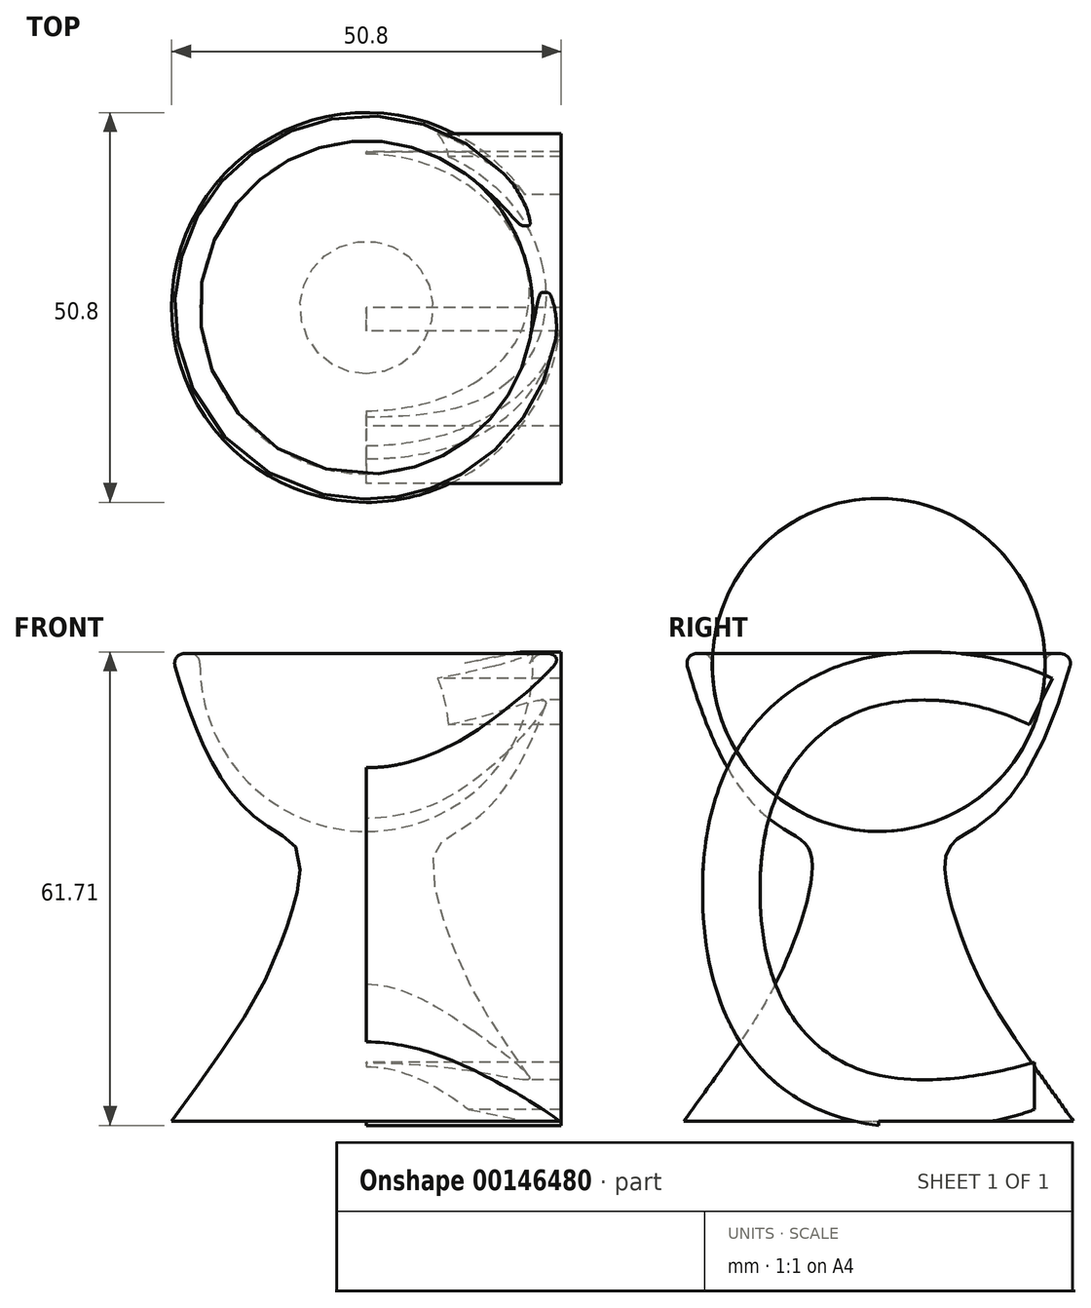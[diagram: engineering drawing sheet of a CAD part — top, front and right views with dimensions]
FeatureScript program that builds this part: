
annotation { "Feature Type Name" : "Feature", "Feature Type Description" : "" }
export const myFeature = defineFeature(function(context is Context, id is Id, definition is map)
    precondition{}
    {
        {
            var Q0;
            Q0=qCreatedBy(makeId("Top.planeOp"),FACE);
            var sketch = newSketch(context, id + "F0", { "sketchPlane" : qUnion([Q0])});
            skCircle(sketch, "E0", {"center": v(0, 0) * mm, "radius": 25.4 * mm});
            skSolve(sketch);
        }
        {
            var Q0;
            Q0 = qSketchRegion(id + "F0", true);
            extrude(context, id + "F1", {"entities" : qUnion([Q0]), "depth" : 60.96 * mm});
        }
        {
            var Q0;
            Q0=qCreatedBy(makeId("Front.planeOp"),FACE);
            var sketch = newSketch(context, id + "F2", { "sketchPlane" : qUnion([Q0])});
            skLineSegment(sketch, "E1", {"start": v(-25.4, 67.56) * mm, "end": v(-25.4, -5.64) * mm});
            skLineSegment(sketch, "E2", {"start": v(0, 70.59) * mm, "end": v(0, -29.87) * mm, "construction": true});
            skLineSegment(sketch, "E3", {"start": v(-48.12, 60.96) * mm, "end": v(45.26, 60.96) * mm, "construction": true});
            skFitSpline(sketch, "E4", {"points": [v(-25.4, 60.96) * mm, v(-8.92, 35.08) * mm, v(-11.78, 21.62) * mm, v(-25.4, 0) * mm], "startDerivative": vector(51.75, -193.24) * mm, "endDerivative": vector(-75.06, -104.5) * mm});
            skLineSegment(sketch, "E5", {"start": v(-25.4, 60.96) * mm, "end": v(-25.4, 0) * mm});
            skSolve(sketch);
        }
        {
            var Q0;
            Q0 = qSketchRegion(id + "F2", true);
            var Q1;
            Q1=sQuery(id+"F2.wireOp",EDGE,"E2");
            revolve(context, id + "F3", {"operationType" : NewBodyOperationType.REMOVE, "entities" : qUnion([Q0]), "axis" : qUnion([Q1]), "revolveType" : RevolveType.FULL, "oppositeDirection" : true});
        }
        {
            var Q0;
            Q0=qCreatedBy(makeId("Right.planeOp"),FACE);
            var sketch = newSketch(context, id + "F4", { "sketchPlane" : qUnion([Q0])});
            skText(sketch, "E6", { "text": "C", "fontName": "OpenSans-Regular.ttf"});
            const initialGuessF4  = {"E6": [-0.02813, 0, 1, 0, 0.06083]};
            skSetInitialGuess(sketch, initialGuessF4);
            skSolve(sketch);
        }
        {
            var Q0;
            Q0 = qSketchRegion(id + "F4", true);
            extrude(context, id + "F5", {"entities" : qUnion([Q0]), "operationType" : NewBodyOperationType.ADD, "depth" : 25.4 * mm});
        }
        {
            var Q0;
            Q0=qCreatedBy(makeId("Front.planeOp"),FACE);
            var sketch = newSketch(context, id + "F6", { "sketchPlane" : qUnion([Q0])});
            skLineSegment(sketch, "E7.bottom", {"start": v(-32.81, -11.53) * mm, "end": v(31.47, -11.53) * mm});
            skLineSegment(sketch, "E7.top", {"start": v(-32.81, 0) * mm, "end": v(31.47, 0) * mm});
            skLineSegment(sketch, "E7.left", {"start": v(-32.81, -11.53) * mm, "end": v(-32.81, 0) * mm});
            skLineSegment(sketch, "E7.right", {"start": v(31.47, -11.53) * mm, "end": v(31.47, 0) * mm});
            skSolve(sketch);
        }
        {
            var Q0;
            Q0=makeQuery(id+"F6.imprint","IMPRINT",FACE,{"disambiguationData":[TD([[makeQuery(id+"F6.imprint","IMPRINT",EDGE,{"derivedFrom":sQuery(id+"F6.wireOp",EDGE,"E7.bottom")}),1.0]])]});
            extrude(context, id + "F7", {"entities" : qUnion([Q0]), "operationType" : NewBodyOperationType.REMOVE, "oppositeDirection" : true, "depth" : 25.4 * mm});
        }
        {
            var Q0;
            Q0=qCreatedBy(makeId("Right.planeOp"),FACE);
            var sketch = newSketch(context, id + "F8", { "sketchPlane" : qUnion([Q0])});
            skArc(sketch, "E8", {"start": v(0, 37.78) * mm, "mid": v(21.7, 59.48) * mm, "end": v(0, 81.19) * mm});
            skLineSegment(sketch, "E9", {"start": v(0, 81.19) * mm, "end": v(0, 37.78) * mm});
            skSolve(sketch);
        }
        {
            var Q0;
            Q0 = qSketchRegion(id + "F8", true);
            var Q1;
            {var subQ0=sQuery(id+"F2.wireOp",EDGE,"E5");var subQ1=sQuery(id+"F2.wireOp",EDGE,"E4");Q1=makeQuery(id+"F3.boolean.opBoolean","MERGE",EDGE,{"derivedFrom":[makeQuery(id+"F1.opExtrude","CAP_EDGE",EDGE,{"disambiguationData":[OSD([sQuery(id+"F0.wireOp",EDGE,"E0")])],"isStart":false}),makeQuery(id+"F3.opRevolve","SWEPT_EDGE",EDGE,{"disambiguationData":[OSD([subQ1,subQ0]),TDD([makeQuery(id+"F2.imprint","INTERSECT",VERTEX,{"disambiguationData":[OD(0.0)],"derivedFrom":[subQ1,subQ0]})])]})]});}
            var Q2;
            Q2 = qConstructionFilter(qBodyType(qCreatedBy(id + "F8" ,EDGE), BodyType.WIRE), ConstructionObject.NO);
            var Q3;
            Q3=sQuery(id+"F8.wireOp",EDGE,"E9");
            revolve(context, id + "F9", {"operationType" : NewBodyOperationType.REMOVE, "entities" : qUnion([Q0]), "surfaceEntities" : qUnion([Q1, Q2]), "axis" : qUnion([Q3]), "revolveType" : RevolveType.FULL, "oppositeDirection" : true});
        }
        {
            var Q0;
            Q0=makeQuery(id+"F9.boolean.opBoolean","INTERSECT",EDGE,{"derivedFrom":[makeQuery(id+"F1.opExtrude","CAP_FACE",FACE,{"disambiguationData":[OSD([sQuery(id+"F0.wireOp",EDGE,"E0")])],"isStart":false}),makeQuery(id+"F9.opRevolve","SWEPT_FACE",FACE,{"disambiguationData":[OSD([sQuery(id+"F8.wireOp",EDGE,"E8")])]})]});
            var Q1;
            {var subQ0=sQuery(id+"F2.wireOp",EDGE,"E5");var subQ1=sQuery(id+"F2.wireOp",EDGE,"E4");Q1=makeQuery(id+"F3.boolean.opBoolean","MERGE",EDGE,{"derivedFrom":[makeQuery(id+"F1.opExtrude","CAP_EDGE",EDGE,{"disambiguationData":[OSD([sQuery(id+"F0.wireOp",EDGE,"E0")])],"isStart":false}),makeQuery(id+"F3.opRevolve","SWEPT_EDGE",EDGE,{"disambiguationData":[OSD([subQ1,subQ0]),TDD([makeQuery(id+"F2.imprint","INTERSECT",VERTEX,{"disambiguationData":[OD(0.0)],"derivedFrom":[subQ1,subQ0]})])]})]});}
            fillet(context, id + "F10", {"entities" : qUnion([Q0, Q1]), "radius" : 1.27 * mm, "tangentPropagation" : true, "allowEdgeOverflow" : false});
        }
    });
